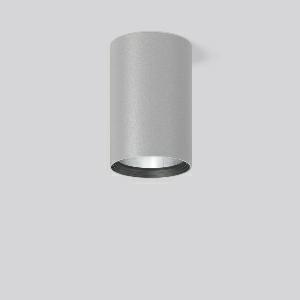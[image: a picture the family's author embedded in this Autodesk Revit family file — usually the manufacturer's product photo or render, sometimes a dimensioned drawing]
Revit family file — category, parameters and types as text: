
# Revit family: heledon_maxi_a_931239_004_76_511c
name_source: partatom
category: Lighting Fixtures
units: mm (PartAtom-declared; Revit-internal decimal feet)

## family parameters
Cut with Voids When Loaded = No
Host = Face
Light Source = No
Part Type = Normal
Room Calculation Point = No
Round Connector Dimension = Use Diameter
Shared = No

## types (1)
- HELEDON maxi A (1 x LED Modul 920 meat+, 2250 lm, 2000)
    Apparent Load = 33 VA
    Approval mark = CE
    CIE Flux Codes = 100 100 100 100 100
    Color Rendering = 90
    Color Temperature = 2000
    Default Elevation = 1800 mm
    Description = Series: HELEDON maxi
Cylindrical surface-mounted downlight. Housing: die-cast aluminium, powder-coated. Internal ceiling frame polycarbonate with bayonet mounting. Black plastic ring and recessed LED to prevent glare from the side. Optical assembly with reflector made of MIRO-Silver with 98% total light reflection for outstanding efficiency - can be changed without tools. Special LED for illumination of meat included. Suitable for Ceiling mounting. Easy installation with a separate ceiling frame with bayonet mounting and plug connection. Driver integrated. Connected via plug-in connector. High quality converter without flickering and stroboscopic effect. The following accessories can be mounted without use of tools: interchangeable lenses, decorative glasses, honeycomb louvre, clear and frosted diffusers, white interchangeable plastic ring. 
Colour: silver
Diameter: 123 mm
Height: 183 mm
Lamp: LED
Socket: without socket
Colour temperature: meat +
System power: 33 W
Rated luminous flux: 2250 lm
Luminous efficiency: 68 lm/W
Control gear: Converter, dimmable, DALI
Protection class: I
Type of protection: IP 20
    Height = 183 mm
    Lamp = 1 x LED Modul 920 meat+
    Lamp Light Flux = 2250 lm
    Lamp count = 1
    Length = 123 mm
    Lifetime = 50000 h
    Luminous efficacy = 68 lm/W
    Manufacturer = RZB
    ModVariant = No
    Model = 931239.004.76
    Mounting Place = Ceiling
    Mounting Type = Surface mounted
    Number of Poles = 1
    OnlyDefault = Yes
    Power Factor = 1
    Product Name = HELEDON maxi A
    Product group = Surface mounted downlights
    ProductGroupID = 302
    Protection Class = Protection class I
    Protection Degree = IP 20
    RLX_Detail_Level = 1
    RLX_Emergency_Light_Flux = 0 lm
    RLX_Emergency_Type = 0
    RLX_Emergency_Type_DB = No
    RlxData = <blob elided: 98117 chars, md5=1b1efeee>
    Socket = socket
    Standby Power = 0 W
    System Light Flux = 2250 lm
    System Power = 33 W
    Type Comments = Product without accessories
    Type Image = 931192.004.jpg
    URL = http://relux.com
    VarID = ---
    Voltage = 230 V
    Voltage Range = 220-240 V
    Weight = 0.00 kg
    Width = 0 mm  [stored 0 ft]

note: [stored X ft] marks values corroborated as IEEE doubles in the binary element streams (Revit-internal decimal feet)

## geometry (parser evidence)
native form markers: Blend x4, Sweep x10
no freeform markers — native parametric forms only
